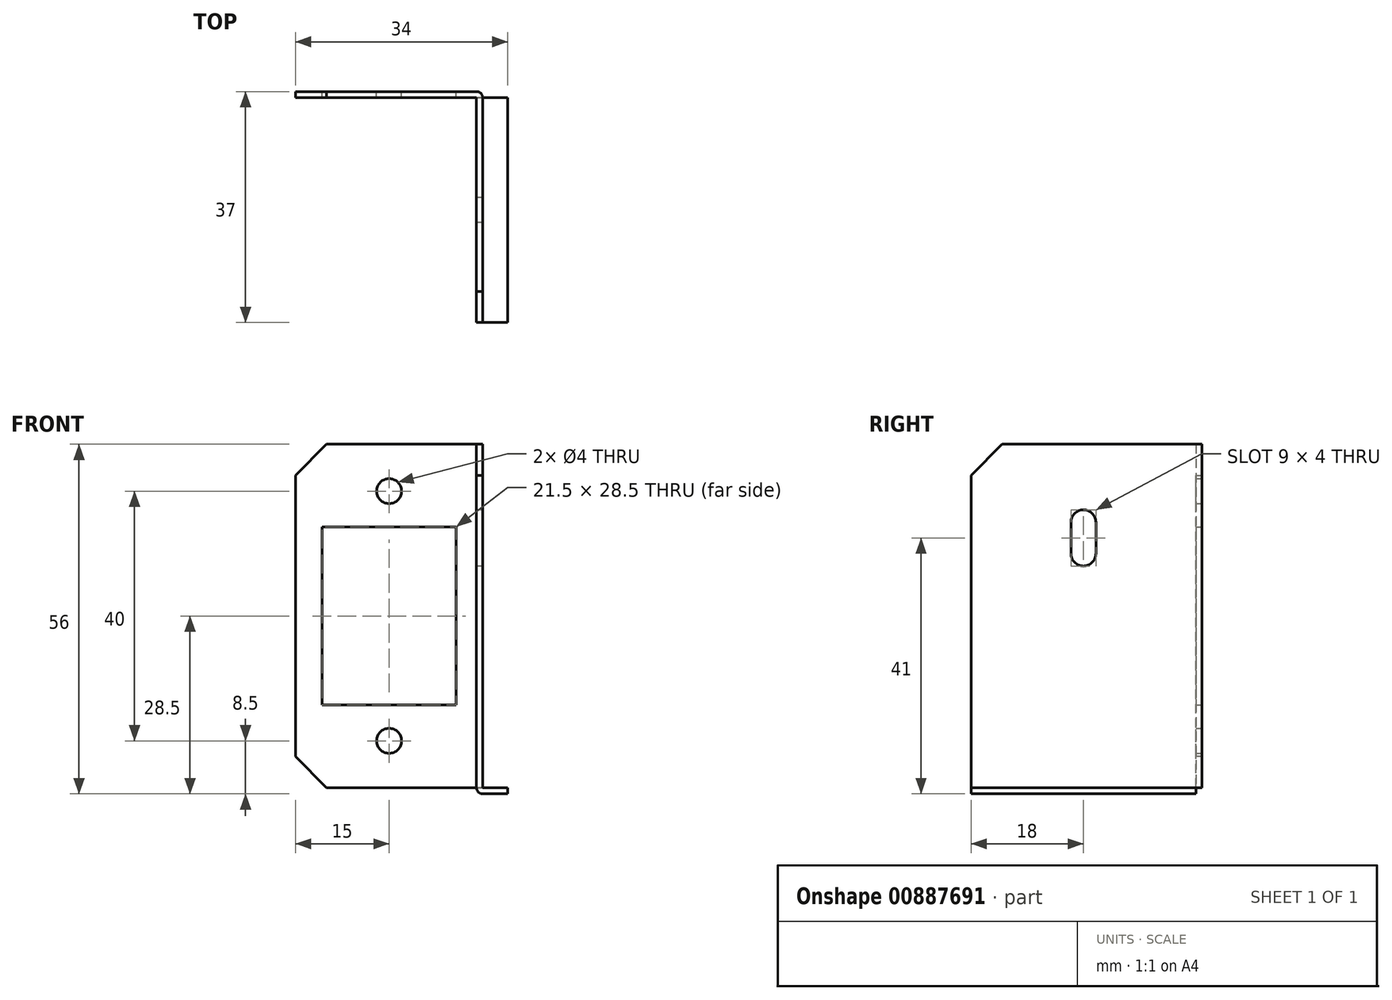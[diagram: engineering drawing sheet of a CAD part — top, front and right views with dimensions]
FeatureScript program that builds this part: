
annotation { "Feature Type Name" : "Feature", "Feature Type Description" : "" }
export const myFeature = defineFeature(function(context is Context, id is Id, definition is map)
    precondition{}
    {
        {
            var Q0;
            Q0=qCreatedBy(makeId("Front.planeOp"),FACE);
            var sketch = newSketch(context, id + "F0", { "sketchPlane" : qUnion([Q0])});
            skLineSegment(sketch, "E0.bottom", {"start": v(0, 0) * mm, "end": v(-30, 0) * mm});
            skLineSegment(sketch, "E0.top", {"start": v(0, 55) * mm, "end": v(-30, 55) * mm});
            skLineSegment(sketch, "E0.left", {"start": v(0, 0) * mm, "end": v(0, 55) * mm});
            skLineSegment(sketch, "E0.right", {"start": v(-30, 0) * mm, "end": v(-30, 55) * mm});
            skLineSegment(sketch, "E1.bottom", {"start": v(-25.75, 41.75) * mm, "end": v(-4.25, 41.75) * mm});
            skLineSegment(sketch, "E1.top", {"start": v(-25.75, 13.25) * mm, "end": v(-4.25, 13.25) * mm});
            skLineSegment(sketch, "E1.left", {"start": v(-25.75, 41.75) * mm, "end": v(-25.75, 13.25) * mm});
            skLineSegment(sketch, "E1.right", {"start": v(-4.25, 41.75) * mm, "end": v(-4.25, 13.25) * mm});
            skPoint(sketch, "E2", {"position": v(-15, 41.75) * mm});
            skPoint(sketch, "E3", {"position": v(-25.75, 27.5) * mm});
            skPoint(sketch, "E4", {"position": v(-15, 55) * mm});
            skPoint(sketch, "E5", {"position": v(-30, 27.5) * mm});
            skCircle(sketch, "E6", {"center": v(-15, 47.5) * mm, "radius": 2 * mm});
            skCircle(sketch, "E7", {"center": v(-15, 7.5) * mm, "radius": 2 * mm});
            skSolve(sketch);
        }
        {
            var Q0;
            Q0 = qSketchRegion(id + "F0", true);
            extrude(context, id + "F1", {"entities" : qUnion([Q0]), "depth" : 1 * mm, "offsetDistance" : 25 * mm});
        }
        {
            var Q0;
            Q0=makeQuery(id+"F1.opExtrude","CAP_FACE",FACE,{"disambiguationData":[OSD([sQuery(id+"F0.wireOp",EDGE,"E0.bottom"),sQuery(id+"F0.wireOp",EDGE,"E0.top"),sQuery(id+"F0.wireOp",EDGE,"E0.left"),sQuery(id+"F0.wireOp",EDGE,"E0.right"),sQuery(id+"F0.wireOp",EDGE,"E1.bottom"),sQuery(id+"F0.wireOp",EDGE,"E1.top"),sQuery(id+"F0.wireOp",EDGE,"E1.left"),sQuery(id+"F0.wireOp",EDGE,"E1.right"),sQuery(id+"F0.wireOp",EDGE,"E6"),sQuery(id+"F0.wireOp",EDGE,"E7")])],"isStart":false});
            var sketch = newSketch(context, id + "F2", { "sketchPlane" : qUnion([Q0])});
            skLineSegment(sketch, "E8", {"start": v(0, 55) * mm, "end": v(-1, 55) * mm});
            skLineSegment(sketch, "E9", {"start": v(-1, 55) * mm, "end": v(-1, -1) * mm});
            skLineSegment(sketch, "E10", {"start": v(-1, -1) * mm, "end": v(4, -1) * mm});
            skLineSegment(sketch, "E11", {"start": v(4, -1) * mm, "end": v(4, 0) * mm});
            skLineSegment(sketch, "E12", {"start": v(4, 0) * mm, "end": v(0, 0) * mm});
            skLineSegment(sketch, "E13", {"start": v(0, 0) * mm, "end": v(0, 55) * mm});
            skSolve(sketch);
        }
        {
            var Q0;
            Q0 = qSketchRegion(id + "F2", true);
            extrude(context, id + "F3", {"entities" : qUnion([Q0]), "operationType" : NewBodyOperationType.ADD, "depth" : 36 * mm, "offsetDistance" : 25 * mm});
        }
        {
            var Q0;
            Q0=makeQuery(id+"F3.opExtrude","SWEPT_FACE",FACE,{"disambiguationData":[OSD([sQuery(id+"F2.wireOp",EDGE,"E9")])]});
            var sketch = newSketch(context, id + "F4", { "sketchPlane" : qUnion([Q0])});
            skLineSegment(sketch, "E14.left", {"start": v(17, 42.5) * mm, "end": v(17, 37.5) * mm});
            skLineSegment(sketch, "E14.right", {"start": v(21, 42.5) * mm, "end": v(21, 37.5) * mm});
            skArc(sketch, "E15", {"start": v(21, 42.5) * mm, "mid": v(19, 44.5) * mm, "end": v(17, 42.5) * mm});
            skArc(sketch, "E16", {"start": v(17, 37.5) * mm, "mid": v(19, 35.5) * mm, "end": v(21, 37.5) * mm});
            skPoint(sketch, "E17", {"position": v(17, 40) * mm});
            skSolve(sketch);
        }
        {
            var Q0;
            Q0 = qSketchRegion(id + "F4", true);
            extrude(context, id + "F5", {"entities" : qUnion([Q0]), "operationType" : NewBodyOperationType.REMOVE, "endBound" : BoundingType.THROUGH_ALL, "oppositeDirection" : true, "depth" : 25 * mm, "offsetDistance" : 25 * mm});
        }
        {
            var Q0;
            Q0=makeQuery(id+"F1.opExtrude","SWEPT_EDGE",EDGE,{"disambiguationData":[OSD([sQuery(id+"F0.wireOp",EDGE,"E0.top"),sQuery(id+"F0.wireOp",EDGE,"E0.right")])]});
            var Q1;
            Q1=makeQuery(id+"F3.opExtrude","CAP_EDGE",EDGE,{"disambiguationData":[OSD([sQuery(id+"F2.wireOp",EDGE,"E8")])],"isStart":false});
            var Q2;
            Q2=makeQuery(id+"F1.opExtrude","SWEPT_EDGE",EDGE,{"disambiguationData":[OSD([sQuery(id+"F0.wireOp",EDGE,"E0.bottom"),sQuery(id+"F0.wireOp",EDGE,"E0.right")])]});
            chamfer(context, id + "F6", {"entities" : qUnion([Q0, Q1, Q2]), "width" : 5 * mm, "tangentPropagation" : true});
        }
        {
            var Q0;
            Q0=makeQuery(id+"F1.opExtrude","CAP_EDGE",EDGE,{"disambiguationData":[OSD([sQuery(id+"F0.wireOp",EDGE,"E0.left")])],"isStart":true});
            var Q1;
            Q1=makeQuery(id+"F3.opExtrude","SWEPT_EDGE",EDGE,{"disambiguationData":[OSD([sQuery(id+"F2.wireOp",EDGE,"E9"),sQuery(id+"F2.wireOp",EDGE,"E10")])]});
            fillet(context, id + "F7", {"entities" : qUnion([Q0, Q1]), "radius" : 1 * mm, "tangentPropagation" : true, "allowEdgeOverflow" : false});
        }
    });
